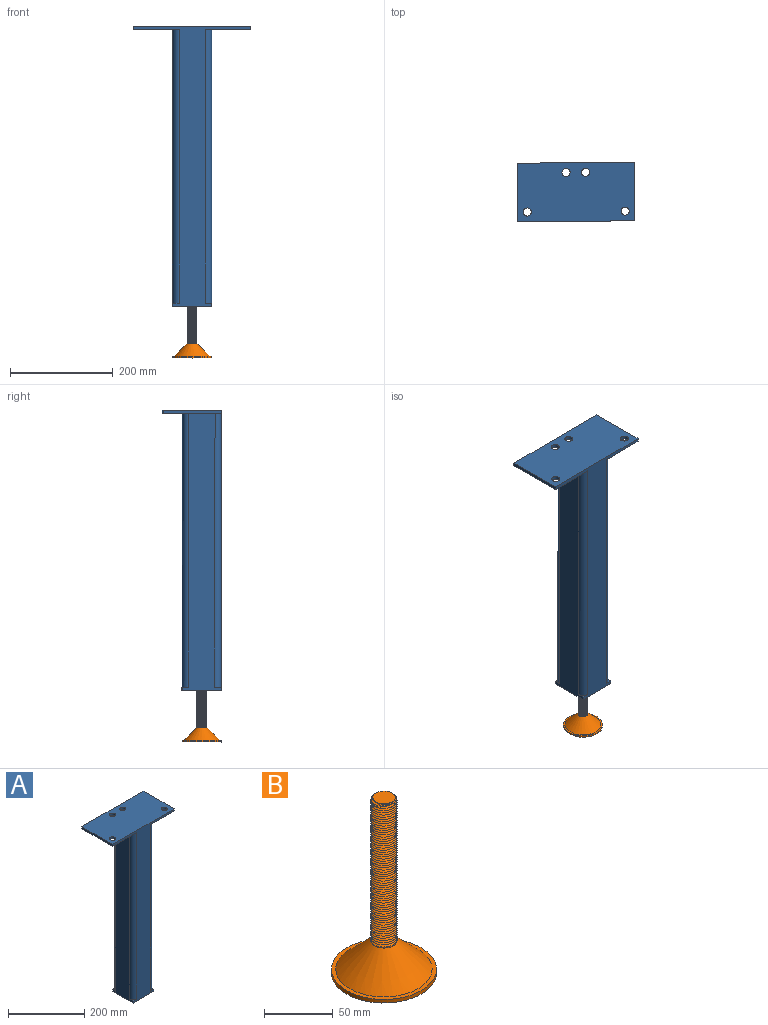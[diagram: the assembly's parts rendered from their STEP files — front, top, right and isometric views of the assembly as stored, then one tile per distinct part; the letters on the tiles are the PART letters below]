
ASSEMBLY  parts=2 mates=1
PART A: 34 faces, bbox 228.6x114.3x546.1 mm
  f0: plane 63.5x63.5mm, normal (0,0,1), area 3712.6mm2, adj f2,f3,f4,f5,f6,f7,f8,f9
  f1: plane 63.5x63.5mm, normal (0,0,-1), area 3997.7mm2, adj f2,f3,f4,f5,f6,f7,f8,f9
  f2: cylinder r=6.35mm len=533.4mm, axis (0,0,-1), area 5320.9mm2, adj f0,f1,f3,f9
  f3: plane 533.4x50.8mm, normal (1,0,0), area 27096.7mm2, adj f0,f1,f2,f4
  f4: cylinder r=6.35mm len=533.4mm, axis (0,0,-1), area 5320.9mm2, adj f0,f1,f3,f5
  f5: plane 533.4x50.8mm, normal (0,-1,0), area 27096.7mm2, adj f0,f1,f4,f6
  f6: cylinder r=6.35mm len=533.4mm, axis (0,0,-1), area 5320.9mm2, adj f0,f1,f5,f7
  f7: plane 533.4x50.8mm, normal (-1,0,0), area 27096.7mm2, adj f0,f1,f6,f8
  f8: cylinder r=6.35mm len=533.4mm, axis (0,0,-1), area 5320.9mm2, adj f0,f1,f7,f9
  f9: plane 533.4x50.8mm, normal (0,1,0), area 27096.7mm2, adj f0,f1,f2,f8
  f10: cylinder r=9.53mm len=19.05mm, axis (0,0,-1), area 304mm2, adj f0,f29
  f11: plane 546.1x228.6mm, normal (0,-1,0), area 29032.2mm2, adj f12,f13,f17,f18,f20,f21,f22,f23
  f12: cylinder r=12.7mm len=533.4mm, axis (0,0,-1), area 10641.8mm2, adj f11,f13,f23,f27
  f13: plane 539.75x76.2mm, normal (-1,0,0), area 27580.6mm2, adj f11,f12,f14,f15,f23,f24,f26,f27
  f14: cylinder r=12.7mm len=533.4mm, axis (0,0,-1), area 10641.8mm2, adj f13,f15,f23,f26
  f15: plane 539.75x76.2mm, normal (0,1,0), area 27580.6mm2, adj f13,f14,f16,f17,f23,f24,f25,f26
  f16: cylinder r=12.7mm len=533.4mm, axis (0,0,-1), area 10641.8mm2, adj f15,f17,f23,f25
  f17: plane 539.75x76.2mm, normal (1,0,0), area 27580.6mm2, adj f11,f15,f16,f18,f23,f24,f25,f28
  f18: cylinder r=12.7mm len=533.4mm, axis (0,0,-1), area 10641.8mm2, adj f11,f17,f23,f28
  f19: plane 228.6x6.35mm, normal (0,1,0), area 1451.6mm2, adj f20,f21,f22,f23
  f20: plane 114.3x6.35mm, normal (1,0,0), area 725.8mm2, adj f11,f19,f22,f23
  f21: plane 114.3x6.35mm, normal (-1,0,0), area 725.8mm2, adj f11,f19,f22,f23
  f22: plane 228.6x114.3mm, normal (0,0,1), area 25337.2mm2, adj f11,f19,f20,f21,f30,f31,f32,f33
  f23: plane 228.6x114.3mm, normal (0,0,-1), area 19669.2mm2, adj f11,f12,f13,f14,f15,f16,f17,f18
  f24: plane 76.2x76.2mm, normal (0,0,-1), area 5440.3mm2, adj f11,f13,f15,f17,f29
  f25: plane 12.7x12.7mm, normal (0,0,1), area 34.6mm2, adj f15,f16,f17
  f26: plane 12.7x12.7mm, normal (0,0,1), area 34.6mm2, adj f13,f14,f15
  f27: plane 12.7x12.7mm, normal (0,0,1), area 34.6mm2, adj f11,f12,f13
  f28: plane 12.7x12.7mm, normal (0,0,1), area 34.6mm2, adj f11,f17,f18
  f29: cone r=9.53mm half-angle=45deg, axis (0,0,-1), area 114.7mm2, adj f10,f24
  f30: cylinder r=7.94mm len=15.88mm, axis (0,0,1), area 316.7mm2, adj f22,f23
  f31: cylinder r=7.94mm len=15.88mm, axis (0,0,1), area 316.7mm2, adj f22,f23
  f32: cylinder r=7.94mm len=15.88mm, axis (0,0,1), area 316.7mm2, adj f22,f23
  f33: cylinder r=7.94mm len=15.88mm, axis (0,0,1), area 316.7mm2, adj f22,f23
PART B: 12 faces, bbox 76.4x76.4x156.8 mm
  f0: plane 76.2x76.2mm, normal (0,0,-1), area 4560.4mm2, adj f1
  f1: cylinder r=38.1mm len=76.2mm, axis (0,0,-1), area 760.1mm2, adj f0,f2
  f2: plane 76.2x76.2mm, normal (0,0,1), area 728.4mm2, adj f1,f3
  f3: cone r=34.92mm half-angle=45deg, axis (0,0,-1), area 5016.1mm2, adj f2,f4,f5
  f4: cylinder r=9.53mm len=19.05mm, axis (0,0,-1), area 39.2mm2, adj f3,f6,f8
  f5: cylinder r=9.53mm len=8.66mm, axis (0,0,-1), area 1.9mm2, adj f3,f6,f8
  f6: plane 1.99x1.76mm, normal (0,1,0), area 1.8mm2, adj f4,f5,f7,f8,f9
  f7: bspline ~127.65x21.84mm, area 6826.9mm2, adj f6,f8,f9,f10,f11
  f8: bspline ~22x19.05mm, area 4.7mm2, adj f4,f5,f6,f7
  f9: bspline ~127.33x21.84mm, area 6773.9mm2, adj f6,f7,f10,f11
  f10: cone r=9.53mm half-angle=45deg, axis (0,0,-1), area 33mm2, adj f7,f9,f11
  f11: plane 16.74x16.57mm, normal (0,0,1), area 210.5mm2, adj f7,f9,f10
PLACE A rot(axis=(0.03,0,1),0.6deg) t=(-63.98,74.73,20.67)mm
PLACE B rot(axis=(0.03,0,1),0.6deg) t=(49.93,114.18,-698.99)mm
MATE cylindrical B.f3 <-> A.f10  axis (0,0,1) through (49.94,114.12,-543.41)mm
